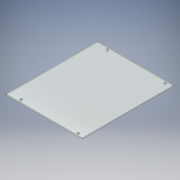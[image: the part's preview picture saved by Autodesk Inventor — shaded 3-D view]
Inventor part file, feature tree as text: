
AUTODESK INVENTOR PART (.ipt)
format: ipt  version: 2019 (Build 230136000, 136)  size: 119,808 bytes
history: native  units: mm
features: extrude x2, sketch x2
ambient origin geometry x8: Origin, YZ Plane, XZ Plane, XY Plane, X Axis, Y Axis, Z Axis, Center Point
bodies: Solid1 (feature_tree)
feature tree (4):
  extrude  "Extrusion1"  Depth=311.0mm
  extrude  "Extrusion2"  TaperAngle=0.0deg  [1 undecoded]
  sketch  "Sketch1"  dims[d0=373.0mm d1=311.0mm]
  sketch  "Sketch2"  dims[d2=300.0mm d3=0.0mm d4=4.0mm d5=0.0mm d6=8.0mm d7=8.0mm d8=9.5mm d9=8.0mm d10=9.5mm d13=12.0mm d14=9.5mm d17=9.5mm d18=4.0mm d19=0.0mm d22=50.0mm d23=235.0mm d24=50.0mm d25=235.0mm]
note: 1 required parameter value undecoded (feature->parameter linkage not recoverable at this tier; creation-order binding heuristic only, values carry confidence <= 0.55)
